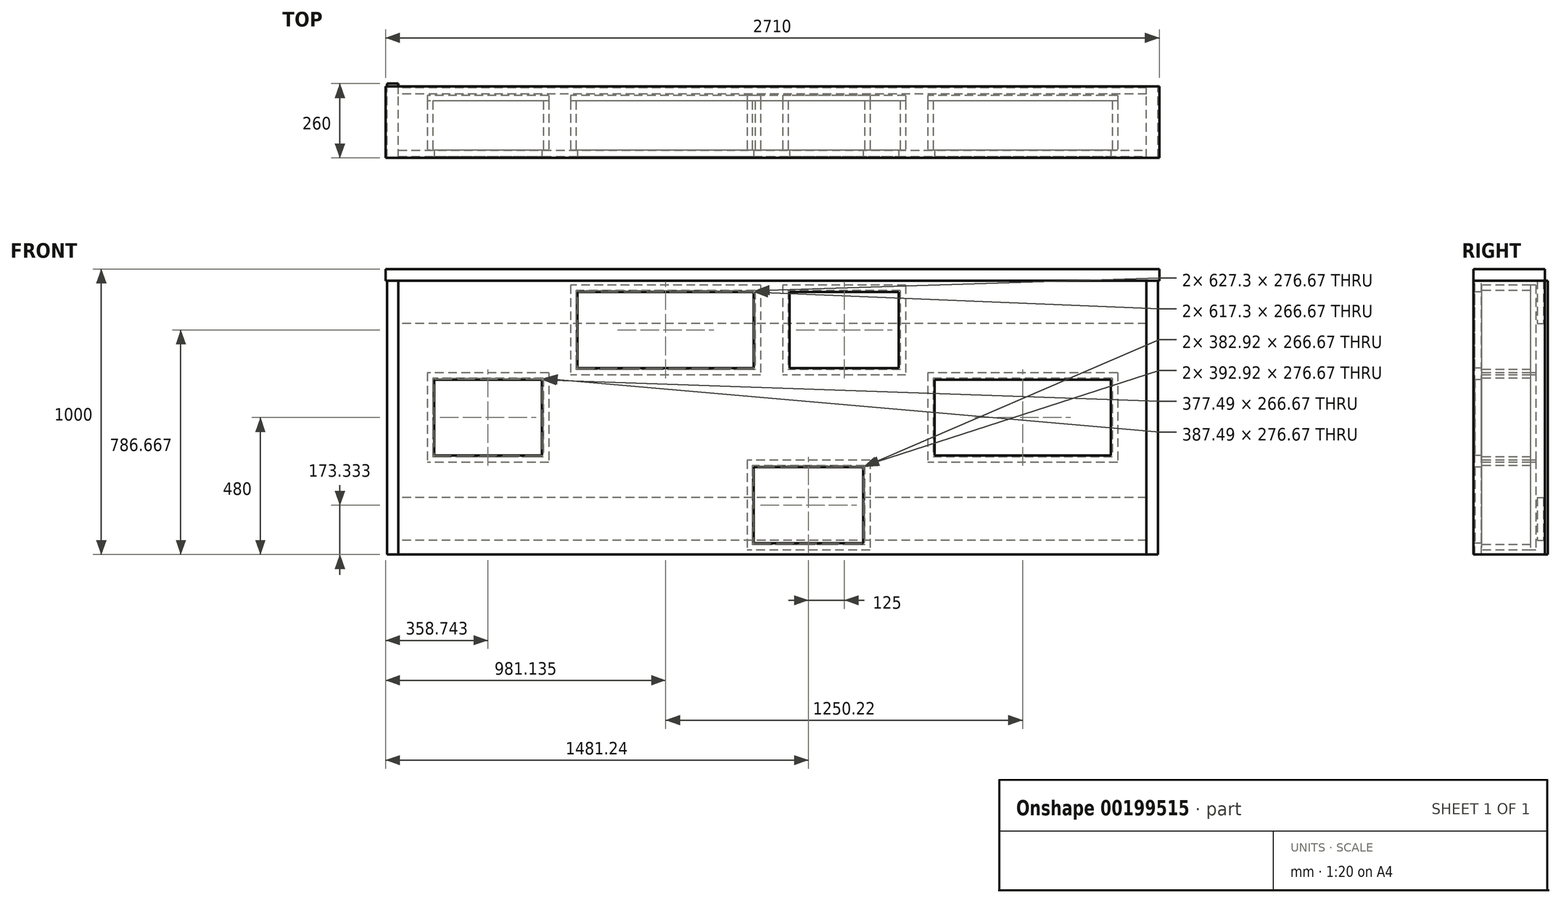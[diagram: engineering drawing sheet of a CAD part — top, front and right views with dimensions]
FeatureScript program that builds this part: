
annotation { "Feature Type Name" : "Feature", "Feature Type Description" : "" }
export const myFeature = defineFeature(function(context is Context, id is Id, definition is map)
    precondition{}
    {
        {
            assignVariable(context, id + "F0", {"name" : "lip", "anyValue" : 5 * mm});
        }
        {
            var Q0;
            Q0=qCreatedBy(makeId("Front.planeOp"),FACE);
            var sketch = newSketch(context, id + "F1", { "sketchPlane" : qUnion([Q0])});
            skLineSegment(sketch, "E0.bottom", {"start": v(0, 0) * mm, "end": v(2620, 0) * mm});
            skLineSegment(sketch, "E0.top", {"start": v(0, 960) * mm, "end": v(2620, 960) * mm});
            skLineSegment(sketch, "E0.left", {"start": v(0, 0) * mm, "end": v(0, 960) * mm});
            skLineSegment(sketch, "E0.right", {"start": v(2620, 0) * mm, "end": v(2620, 960) * mm});
            skSolve(sketch);
        }
        {
            var Q0;
            Q0=qSketchRegion(id+"F1",true);
            extrude(context, id + "F2", {"entities" : qUnion([Q0]), "depth" : 22 * mm});
        }
        {
            var Q0;
            Q0=makeQuery(id+"F2.opExtrude","CAP_FACE",FACE,{"disambiguationData":[OSD([sQuery(id+"F1.wireOp",EDGE,"E0.bottom"),sQuery(id+"F1.wireOp",EDGE,"E0.top"),sQuery(id+"F1.wireOp",EDGE,"E0.left"),sQuery(id+"F1.wireOp",EDGE,"E0.right")])],"isStart":false});
            var sketch = newSketch(context, id + "F3", { "sketchPlane" : qUnion([Q0])});
            skLineSegment(sketch, "E1.bottom", {"start": v(0, 653.33) * mm, "end": v(2620, 653.33) * mm, "construction": true});
            skLineSegment(sketch, "E1.top", {"start": v(0, 613.33) * mm, "end": v(2620, 613.33) * mm, "construction": true});
            skLineSegment(sketch, "E1.left", {"start": v(0, 653.33) * mm, "end": v(0, 613.33) * mm, "construction": true});
            skLineSegment(sketch, "E1.right", {"start": v(2620, 653.33) * mm, "end": v(2620, 613.33) * mm, "construction": true});
            skLineSegment(sketch, "E2.bottom", {"start": v(0, 346.67) * mm, "end": v(2620, 346.67) * mm, "construction": true});
            skLineSegment(sketch, "E2.top", {"start": v(0, 306.67) * mm, "end": v(2620, 306.67) * mm, "construction": true});
            skLineSegment(sketch, "E2.left", {"start": v(0, 346.67) * mm, "end": v(0, 306.67) * mm, "construction": true});
            skLineSegment(sketch, "E2.right", {"start": v(2620, 346.67) * mm, "end": v(2620, 306.67) * mm, "construction": true});
            skLineSegment(sketch, "E3.bottom", {"start": v(0, 960) * mm, "end": v(2620, 960) * mm, "construction": true});
            skLineSegment(sketch, "E3.top", {"start": v(0, 920) * mm, "end": v(2620, 920) * mm, "construction": true});
            skLineSegment(sketch, "E3.left", {"start": v(0, 960) * mm, "end": v(0, 920) * mm, "construction": true});
            skLineSegment(sketch, "E3.right", {"start": v(2620, 960) * mm, "end": v(2620, 920) * mm, "construction": true});
            skLineSegment(sketch, "E4.bottom", {"start": v(0, 0) * mm, "end": v(2620, 0) * mm, "construction": true});
            skLineSegment(sketch, "E4.top", {"start": v(0, 40) * mm, "end": v(2620, 40) * mm, "construction": true});
            skLineSegment(sketch, "E4.left", {"start": v(0, 0) * mm, "end": v(0, 40) * mm, "construction": true});
            skLineSegment(sketch, "E4.right", {"start": v(2620, 0) * mm, "end": v(2620, 40) * mm, "construction": true});
            skLineSegment(sketch, "E5", {"start": v(2533.8, 920) * mm, "end": v(2533.8, 653.33) * mm, "construction": true});
            skLineSegment(sketch, "E6", {"start": v(2533.8, 613.33) * mm, "end": v(2533.8, 346.67) * mm, "construction": true});
            skLineSegment(sketch, "E7", {"start": v(2533.8, 306.67) * mm, "end": v(2533.8, 40) * mm, "construction": true});
            skLineSegment(sketch, "E8.bottom", {"start": v(125, 613.33) * mm, "end": v(502.49, 613.33) * mm});
            skLineSegment(sketch, "E8.top", {"start": v(125, 346.67) * mm, "end": v(502.49, 346.67) * mm});
            skLineSegment(sketch, "E8.left", {"start": v(125, 613.33) * mm, "end": v(125, 346.67) * mm});
            skLineSegment(sketch, "E8.right", {"start": v(502.49, 613.33) * mm, "end": v(502.49, 346.67) * mm});
            skLineSegment(sketch, "E9.bottom", {"start": v(627.49, 653.33) * mm, "end": v(1244.78, 653.33) * mm});
            skLineSegment(sketch, "E9.top", {"start": v(627.49, 920) * mm, "end": v(1244.78, 920) * mm});
            skLineSegment(sketch, "E9.left", {"start": v(627.49, 653.33) * mm, "end": v(627.49, 920) * mm});
            skLineSegment(sketch, "E9.right", {"start": v(1244.78, 653.33) * mm, "end": v(1244.78, 920) * mm});
            skLineSegment(sketch, "E10.bottom", {"start": v(1369.78, 920) * mm, "end": v(1752.7, 920) * mm});
            skLineSegment(sketch, "E10.top", {"start": v(1369.78, 653.33) * mm, "end": v(1752.7, 653.33) * mm});
            skLineSegment(sketch, "E10.left", {"start": v(1369.78, 920) * mm, "end": v(1369.78, 653.33) * mm});
            skLineSegment(sketch, "E10.right", {"start": v(1752.7, 920) * mm, "end": v(1752.7, 653.33) * mm});
            skLineSegment(sketch, "E11.bottom", {"start": v(1244.78, 306.67) * mm, "end": v(1627.7, 306.67) * mm});
            skLineSegment(sketch, "E11.top", {"start": v(1244.78, 40) * mm, "end": v(1627.7, 40) * mm});
            skLineSegment(sketch, "E11.left", {"start": v(1244.78, 306.67) * mm, "end": v(1244.78, 40) * mm});
            skLineSegment(sketch, "E11.right", {"start": v(1627.7, 306.67) * mm, "end": v(1627.7, 40) * mm});
            skLineSegment(sketch, "E12.bottom", {"start": v(1877.7, 613.33) * mm, "end": v(2495, 613.33) * mm});
            skLineSegment(sketch, "E12.top", {"start": v(1877.7, 346.67) * mm, "end": v(2495, 346.67) * mm});
            skLineSegment(sketch, "E12.left", {"start": v(1877.7, 613.33) * mm, "end": v(1877.7, 346.67) * mm});
            skLineSegment(sketch, "E12.right", {"start": v(2495, 613.33) * mm, "end": v(2495, 346.67) * mm});
            skLineSegment(sketch, "E13", {"start": v(627.49, 821.36) * mm, "end": v(1244.78, 821.36) * mm, "construction": true});
            skPoint(sketch, "E13.endSnap0", {"position": v(1244.78, 786.67) * mm});
            skLineSegment(sketch, "E14", {"start": v(1877.7, 480) * mm, "end": v(2495, 480) * mm, "construction": true});
            skSolve(sketch);
        }
        {
            var Q0;
            Q0=qSketchRegion(id+"F3",true);
            extrude(context, id + "F4", {"entities" : qUnion([Q0]), "operationType" : NewBodyOperationType.REMOVE, "endBound" : BoundingType.UP_TO_NEXT, "oppositeDirection" : true, "depth" : 25 * mm});
        }
        {
            var Q0;
            Q0=makeQuery(id+"F2.opExtrude","CAP_FACE",FACE,{"disambiguationData":[OSD([sQuery(id+"F1.wireOp",EDGE,"E0.bottom"),sQuery(id+"F1.wireOp",EDGE,"E0.top"),sQuery(id+"F1.wireOp",EDGE,"E0.left"),sQuery(id+"F1.wireOp",EDGE,"E0.right")])],"isStart":false});
            var sketch = newSketch(context, id + "F5", { "sketchPlane" : qUnion([Q0])});
            skLineSegment(sketch, "E15.bottom", {"start": v(-45, 1000) * mm, "end": v(2665, 1000) * mm});
            skLineSegment(sketch, "E15.top", {"start": v(-45, 960) * mm, "end": v(2665, 960) * mm});
            skLineSegment(sketch, "E15.left", {"start": v(-45, 1000) * mm, "end": v(-45, 960) * mm});
            skLineSegment(sketch, "E15.right", {"start": v(2665, 1000) * mm, "end": v(2665, 960) * mm});
            skLineSegment(sketch, "E16.bottom", {"start": v(2620, 0) * mm, "end": v(2660, 0) * mm});
            skLineSegment(sketch, "E16.top", {"start": v(2620, 960) * mm, "end": v(2660, 960) * mm});
            skLineSegment(sketch, "E16.left", {"start": v(2620, 0) * mm, "end": v(2620, 960) * mm});
            skLineSegment(sketch, "E16.right", {"start": v(2660, 0) * mm, "end": v(2660, 960) * mm});
            skLineSegment(sketch, "E17.bottom", {"start": v(0, 0) * mm, "end": v(-40, 0) * mm});
            skLineSegment(sketch, "E17.top", {"start": v(0, 960) * mm, "end": v(-40, 960) * mm});
            skLineSegment(sketch, "E17.left", {"start": v(0, 0) * mm, "end": v(0, 960) * mm});
            skLineSegment(sketch, "E17.right", {"start": v(-40, 0) * mm, "end": v(-40, 960) * mm});
            skSolve(sketch);
        }
        {
            var Q0;
            Q0=makeQuery(id+"F5.imprint","IMPRINT",FACE,{"disambiguationData":[TD([[makeQuery(id+"F5.imprint","IMPRINT",EDGE,{"derivedFrom":sQuery(id+"F5.wireOp",EDGE,"E17.bottom")}),-1.0]])]});
            extrude(context, id + "F6", {"entities" : qUnion([Q0]), "depth" : getVariable(context, 'lip'), "hasSecondDirection" : true, "secondDirectionOppositeDirection" : true, "secondDirectionDepth" : 255 * mm});
        }
        {
            var Q0;
            Q0=makeQuery(id+"F5.imprint","IMPRINT",FACE,{"disambiguationData":[TD([[makeQuery(id+"F5.imprint","IMPRINT",EDGE,{"derivedFrom":sQuery(id+"F5.wireOp",EDGE,"E16.bottom")}),1.0]])]});
            extrude(context, id + "F7", {"entities" : qUnion([Q0]), "depth" : getVariable(context, 'lip'), "hasSecondDirection" : true, "secondDirectionOppositeDirection" : true, "secondDirectionDepth" : 250 * mm - getVariable(context, 'lip')});
        }
        {
            var Q0;
            Q0=makeQuery(id+"F5.imprint","IMPRINT",FACE,{"disambiguationData":[TD([[makeQuery(id+"F5.imprint","IMPRINT",EDGE,{"derivedFrom":sQuery(id+"F5.wireOp",EDGE,"E15.bottom")}),-1.0]])]});
            extrude(context, id + "F8", {"entities" : qUnion([Q0]), "depth" : getVariable(context, 'lip'), "hasSecondDirection" : true, "secondDirectionOppositeDirection" : true, "secondDirectionDepth" : 250 * mm - getVariable(context, 'lip')});
        }
        {
            var Q0;
            Q0=makeQuery(id+"F2.opExtrude","CAP_FACE",FACE,{"disambiguationData":[OSD([sQuery(id+"F1.wireOp",EDGE,"E0.bottom"),sQuery(id+"F1.wireOp",EDGE,"E0.top"),sQuery(id+"F1.wireOp",EDGE,"E0.left"),sQuery(id+"F1.wireOp",EDGE,"E0.right")])],"isStart":true});
            var sketch = newSketch(context, id + "F9", { "sketchPlane" : qUnion([Q0])});
            skLineSegment(sketch, "E18.bottom", {"start": v(-2500, 618.33) * mm, "end": v(-1872.7, 618.33) * mm});
            skLineSegment(sketch, "E18.top", {"start": v(-2500, 341.67) * mm, "end": v(-1872.7, 341.67) * mm});
            skLineSegment(sketch, "E18.left", {"start": v(-2500, 618.33) * mm, "end": v(-2500, 341.67) * mm});
            skLineSegment(sketch, "E18.right", {"start": v(-1872.7, 618.33) * mm, "end": v(-1872.7, 341.67) * mm});
            skLineSegment(sketch, "E19.0", {"start": v(-2519, 637.33) * mm, "end": v(-1853.7, 637.33) * mm});
            skLineSegment(sketch, "E19.1", {"start": v(-2519, 637.33) * mm, "end": v(-2519, 322.67) * mm});
            skLineSegment(sketch, "E19.2", {"start": v(-2519, 322.67) * mm, "end": v(-1853.7, 322.67) * mm});
            skLineSegment(sketch, "E19.3", {"start": v(-1853.7, 637.33) * mm, "end": v(-1853.7, 322.67) * mm});
            skLineSegment(sketch, "E20", {"start": v(-2186.35, 618.33) * mm, "end": v(-2186.35, 613.33) * mm, "construction": true});
            skLineSegment(sketch, "E21", {"start": v(-2186.35, 613.33) * mm, "end": v(-1877.7, 480) * mm, "construction": true});
            skPoint(sketch, "E21.endSnap0", {"position": v(-1872.7, 480) * mm});
            skLineSegment(sketch, "E22", {"start": v(-1877.7, 480) * mm, "end": v(-1872.7, 480) * mm, "construction": true});
            skLineSegment(sketch, "E23", {"start": v(-2500, 480) * mm, "end": v(-2495, 480) * mm, "construction": true});
            skPoint(sketch, "E23.endSnap0", {"position": v(-2500, 480) * mm});
            skLineSegment(sketch, "E24", {"start": v(-2495, 480) * mm, "end": v(-2186.35, 346.67) * mm, "construction": true});
            skLineSegment(sketch, "E25", {"start": v(-2186.35, 346.67) * mm, "end": v(-2186.35, 341.67) * mm, "construction": true});
            skLineSegment(sketch, "E26.bottom", {"start": v(-1757.7, 925) * mm, "end": v(-1364.78, 925) * mm});
            skLineSegment(sketch, "E26.top", {"start": v(-1757.7, 648.33) * mm, "end": v(-1364.78, 648.33) * mm});
            skLineSegment(sketch, "E26.left", {"start": v(-1757.7, 925) * mm, "end": v(-1757.7, 648.33) * mm});
            skLineSegment(sketch, "E26.right", {"start": v(-1364.78, 925) * mm, "end": v(-1364.78, 648.33) * mm});
            skLineSegment(sketch, "E27.0", {"start": v(-1776.7, 944) * mm, "end": v(-1345.78, 944) * mm});
            skLineSegment(sketch, "E27.1", {"start": v(-1776.7, 944) * mm, "end": v(-1776.7, 629.33) * mm});
            skLineSegment(sketch, "E27.2", {"start": v(-1776.7, 629.33) * mm, "end": v(-1345.78, 629.33) * mm});
            skLineSegment(sketch, "E27.3", {"start": v(-1345.78, 944) * mm, "end": v(-1345.78, 629.33) * mm});
            skLineSegment(sketch, "E28", {"start": v(-1561.24, 925) * mm, "end": v(-1561.24, 920) * mm, "construction": true});
            skLineSegment(sketch, "E29", {"start": v(-1561.24, 920) * mm, "end": v(-1369.78, 786.67) * mm, "construction": true});
            skPoint(sketch, "E29.endSnap0", {"position": v(-1364.78, 786.67) * mm});
            skLineSegment(sketch, "E30", {"start": v(-1369.78, 786.67) * mm, "end": v(-1364.78, 786.67) * mm, "construction": true});
            skLineSegment(sketch, "E31", {"start": v(-1757.7, 786.67) * mm, "end": v(-1752.7, 786.67) * mm, "construction": true});
            skPoint(sketch, "E31.endSnap0", {"position": v(-1757.7, 786.67) * mm});
            skLineSegment(sketch, "E32", {"start": v(-1752.7, 786.67) * mm, "end": v(-1561.24, 653.33) * mm, "construction": true});
            skLineSegment(sketch, "E33", {"start": v(-1561.24, 653.33) * mm, "end": v(-1561.24, 648.33) * mm, "construction": true});
            skLineSegment(sketch, "E34.bottom", {"start": v(-1249.78, 925) * mm, "end": v(-622.49, 925) * mm});
            skLineSegment(sketch, "E34.top", {"start": v(-1249.78, 648.33) * mm, "end": v(-622.49, 648.33) * mm});
            skLineSegment(sketch, "E34.left", {"start": v(-1249.78, 925) * mm, "end": v(-1249.78, 648.33) * mm});
            skLineSegment(sketch, "E34.right", {"start": v(-622.49, 925) * mm, "end": v(-622.49, 648.33) * mm});
            skLineSegment(sketch, "E35.0", {"start": v(-1268.78, 944) * mm, "end": v(-603.49, 944) * mm});
            skLineSegment(sketch, "E35.1", {"start": v(-1268.78, 944) * mm, "end": v(-1268.78, 629.33) * mm});
            skLineSegment(sketch, "E35.2", {"start": v(-1268.78, 629.33) * mm, "end": v(-603.49, 629.33) * mm});
            skLineSegment(sketch, "E35.3", {"start": v(-603.49, 944) * mm, "end": v(-603.49, 629.33) * mm});
            skLineSegment(sketch, "E36", {"start": v(-936.13, 925) * mm, "end": v(-936.13, 920) * mm, "construction": true});
            skLineSegment(sketch, "E37", {"start": v(-936.13, 920) * mm, "end": v(-627.49, 786.67) * mm, "construction": true});
            skPoint(sketch, "E37.endSnap0", {"position": v(-622.49, 786.67) * mm});
            skLineSegment(sketch, "E38", {"start": v(-627.49, 786.67) * mm, "end": v(-622.49, 786.67) * mm, "construction": true});
            skLineSegment(sketch, "E39", {"start": v(-1249.78, 786.67) * mm, "end": v(-1244.78, 786.67) * mm, "construction": true});
            skPoint(sketch, "E39.endSnap0", {"position": v(-1249.78, 786.67) * mm});
            skLineSegment(sketch, "E40", {"start": v(-1244.78, 786.67) * mm, "end": v(-936.13, 653.33) * mm, "construction": true});
            skLineSegment(sketch, "E41", {"start": v(-936.13, 653.33) * mm, "end": v(-936.13, 648.33) * mm, "construction": true});
            skLineSegment(sketch, "E42.bottom", {"start": v(-507.49, 618.33) * mm, "end": v(-120, 618.33) * mm});
            skLineSegment(sketch, "E42.top", {"start": v(-507.49, 341.67) * mm, "end": v(-120, 341.67) * mm});
            skLineSegment(sketch, "E42.left", {"start": v(-507.49, 618.33) * mm, "end": v(-507.49, 341.67) * mm});
            skLineSegment(sketch, "E42.right", {"start": v(-120, 618.33) * mm, "end": v(-120, 341.67) * mm});
            skLineSegment(sketch, "E43.0", {"start": v(-526.49, 637.33) * mm, "end": v(-101, 637.33) * mm});
            skLineSegment(sketch, "E43.1", {"start": v(-526.49, 637.33) * mm, "end": v(-526.49, 322.67) * mm});
            skLineSegment(sketch, "E43.2", {"start": v(-526.49, 322.67) * mm, "end": v(-101, 322.67) * mm});
            skLineSegment(sketch, "E43.3", {"start": v(-101, 637.33) * mm, "end": v(-101, 322.67) * mm});
            skLineSegment(sketch, "E44", {"start": v(-313.74, 618.33) * mm, "end": v(-313.74, 613.33) * mm, "construction": true});
            skLineSegment(sketch, "E45", {"start": v(-313.74, 613.33) * mm, "end": v(-125, 480) * mm, "construction": true});
            skPoint(sketch, "E45.endSnap0", {"position": v(-120, 480) * mm});
            skLineSegment(sketch, "E46", {"start": v(-125, 480) * mm, "end": v(-120, 480) * mm, "construction": true});
            skLineSegment(sketch, "E47", {"start": v(-507.49, 480) * mm, "end": v(-502.49, 480) * mm, "construction": true});
            skPoint(sketch, "E47.endSnap0", {"position": v(-507.49, 480) * mm});
            skLineSegment(sketch, "E48", {"start": v(-502.49, 480) * mm, "end": v(-313.74, 346.67) * mm, "construction": true});
            skLineSegment(sketch, "E49", {"start": v(-313.74, 346.67) * mm, "end": v(-313.74, 341.67) * mm, "construction": true});
            skLineSegment(sketch, "E50.bottom", {"start": v(-1632.7, 311.67) * mm, "end": v(-1239.78, 311.67) * mm});
            skLineSegment(sketch, "E50.top", {"start": v(-1632.7, 35) * mm, "end": v(-1239.78, 35) * mm});
            skLineSegment(sketch, "E50.left", {"start": v(-1632.7, 311.67) * mm, "end": v(-1632.7, 35) * mm});
            skLineSegment(sketch, "E50.right", {"start": v(-1239.78, 311.67) * mm, "end": v(-1239.78, 35) * mm});
            skLineSegment(sketch, "E51.0", {"start": v(-1651.7, 330.67) * mm, "end": v(-1220.78, 330.67) * mm});
            skLineSegment(sketch, "E51.1", {"start": v(-1651.7, 330.67) * mm, "end": v(-1651.7, 16) * mm});
            skLineSegment(sketch, "E51.2", {"start": v(-1651.7, 16) * mm, "end": v(-1220.78, 16) * mm});
            skLineSegment(sketch, "E51.3", {"start": v(-1220.78, 330.67) * mm, "end": v(-1220.78, 16) * mm});
            skLineSegment(sketch, "E52", {"start": v(-1436.24, 311.67) * mm, "end": v(-1436.24, 306.67) * mm, "construction": true});
            skLineSegment(sketch, "E53", {"start": v(-1436.24, 306.67) * mm, "end": v(-1244.78, 173.33) * mm, "construction": true});
            skPoint(sketch, "E53.endSnap0", {"position": v(-1239.78, 173.33) * mm});
            skLineSegment(sketch, "E54", {"start": v(-1244.78, 173.33) * mm, "end": v(-1239.78, 173.33) * mm, "construction": true});
            skLineSegment(sketch, "E55", {"start": v(-1632.7, 173.33) * mm, "end": v(-1627.7, 173.33) * mm, "construction": true});
            skPoint(sketch, "E55.endSnap0", {"position": v(-1632.7, 173.33) * mm});
            skLineSegment(sketch, "E56", {"start": v(-1627.7, 173.33) * mm, "end": v(-1436.24, 40) * mm, "construction": true});
            skLineSegment(sketch, "E57", {"start": v(-1436.24, 40) * mm, "end": v(-1436.24, 35) * mm, "construction": true});
            skSolve(sketch);
        }
        {
            var Q0;
            Q0=qSketchRegion(id+"F9",true);
            extrude(context, id + "F10", {"entities" : qUnion([Q0]), "depth" : 172 * mm});
        }
        {
            var Q0;
            Q0=makeQuery(id+"F10.opExtrude","CAP_FACE",FACE,{"disambiguationData":[OSD([sQuery(id+"F9.wireOp",EDGE,"E18.bottom"),sQuery(id+"F9.wireOp",EDGE,"E18.top"),sQuery(id+"F9.wireOp",EDGE,"E18.left"),sQuery(id+"F9.wireOp",EDGE,"E18.right"),sQuery(id+"F9.wireOp",EDGE,"E19.0"),sQuery(id+"F9.wireOp",EDGE,"E19.1"),sQuery(id+"F9.wireOp",EDGE,"E19.2"),sQuery(id+"F9.wireOp",EDGE,"E19.3")])],"isStart":false});
            var sketch = newSketch(context, id + "F11", { "sketchPlane" : qUnion([Q0])});
            skLineSegment(sketch, "E58.0", {"start": v(-2519, 637.33) * mm, "end": v(-1853.7, 637.33) * mm});
            skLineSegment(sketch, "E59.0", {"start": v(-2519, 637.33) * mm, "end": v(-2519, 322.67) * mm});
            skLineSegment(sketch, "E60.0", {"start": v(-2519, 322.67) * mm, "end": v(-1853.7, 322.67) * mm});
            skLineSegment(sketch, "E61.0", {"start": v(-1853.7, 637.33) * mm, "end": v(-1853.7, 322.67) * mm});
            skLineSegment(sketch, "E62.0", {"start": v(-1776.7, 944) * mm, "end": v(-1776.7, 629.33) * mm});
            skLineSegment(sketch, "E63.0", {"start": v(-1776.7, 944) * mm, "end": v(-1345.78, 944) * mm});
            skLineSegment(sketch, "E64.0", {"start": v(-1345.78, 944) * mm, "end": v(-1345.78, 629.33) * mm});
            skLineSegment(sketch, "E65.0", {"start": v(-1776.7, 629.33) * mm, "end": v(-1345.78, 629.33) * mm});
            skLineSegment(sketch, "E66.0", {"start": v(-1268.78, 944) * mm, "end": v(-1268.78, 629.33) * mm});
            skLineSegment(sketch, "E67.0", {"start": v(-1268.78, 944) * mm, "end": v(-603.49, 944) * mm});
            skLineSegment(sketch, "E68.0", {"start": v(-603.49, 944) * mm, "end": v(-603.49, 629.33) * mm});
            skLineSegment(sketch, "E69.0", {"start": v(-1268.78, 629.33) * mm, "end": v(-603.49, 629.33) * mm});
            skLineSegment(sketch, "E70.0", {"start": v(-1220.78, 330.67) * mm, "end": v(-1220.78, 16) * mm});
            skLineSegment(sketch, "E71.0", {"start": v(-1651.7, 330.67) * mm, "end": v(-1220.78, 330.67) * mm});
            skLineSegment(sketch, "E72.0", {"start": v(-1651.7, 330.67) * mm, "end": v(-1651.7, 16) * mm});
            skLineSegment(sketch, "E73.0", {"start": v(-1651.7, 16) * mm, "end": v(-1220.78, 16) * mm});
            skLineSegment(sketch, "E74.0", {"start": v(-526.49, 637.33) * mm, "end": v(-101, 637.33) * mm});
            skLineSegment(sketch, "E75.0", {"start": v(-526.49, 637.33) * mm, "end": v(-526.49, 322.67) * mm});
            skLineSegment(sketch, "E76.0", {"start": v(-526.49, 322.67) * mm, "end": v(-101, 322.67) * mm});
            skLineSegment(sketch, "E77.0", {"start": v(-101, 637.33) * mm, "end": v(-101, 322.67) * mm});
            skSolve(sketch);
        }
        {
            var Q0;
            Q0=qSketchRegion(id+"F11",true);
            extrude(context, id + "F12", {"entities" : qUnion([Q0]), "depth" : 19 * mm});
        }
        {
            var Q0;
            Q0=makeQuery(id+"F8.opExtrude","CAP_FACE",FACE,{"disambiguationData":[OSD([sQuery(id+"F5.wireOp",EDGE,"E15.bottom"),sQuery(id+"F5.wireOp",EDGE,"E15.top"),sQuery(id+"F5.wireOp",EDGE,"E15.left"),sQuery(id+"F5.wireOp",EDGE,"E15.right"),sQuery(id+"F5.wireOp",EDGE,"E16.top"),sQuery(id+"F5.wireOp",EDGE,"E17.top")])],"isStart":true});
            cPlane(context, id + "F13", {"entities" : qUnion([Q0]), "cplaneType" : CPlaneType.OFFSET, "offset" : getVariable(context, 'lip'), "oppositeDirection" : true, "width" : 150 * mm, "height" : 150 * mm});
        }
        {
            var Q0;
            Q0=qCreatedBy(id+"F13.planeOp",FACE);
            var sketch = newSketch(context, id + "F14", { "sketchPlane" : qUnion([Q0])});
            skLineSegment(sketch, "E78.bottom", {"start": v(-2620, 960) * mm, "end": v(0, 960) * mm});
            skLineSegment(sketch, "E78.top", {"start": v(-2620, 810) * mm, "end": v(0, 810) * mm});
            skLineSegment(sketch, "E78.left", {"start": v(-2620, 960) * mm, "end": v(-2620, 810) * mm});
            skLineSegment(sketch, "E78.right", {"start": v(0, 960) * mm, "end": v(0, 810) * mm});
            skLineSegment(sketch, "E79.bottom", {"start": v(-2620, 200) * mm, "end": v(0, 200) * mm});
            skLineSegment(sketch, "E79.top", {"start": v(-2620, 50) * mm, "end": v(0, 50) * mm});
            skLineSegment(sketch, "E79.left", {"start": v(-2620, 200) * mm, "end": v(-2620, 50) * mm});
            skLineSegment(sketch, "E79.right", {"start": v(0, 200) * mm, "end": v(0, 50) * mm});
            skSolve(sketch);
        }
        {
            var Q0;
            Q0=qSketchRegion(id+"F14",true);
            extrude(context, id + "F15", {"entities" : qUnion([Q0]), "oppositeDirection" : true, "depth" : 22 * mm});
        }
    });
